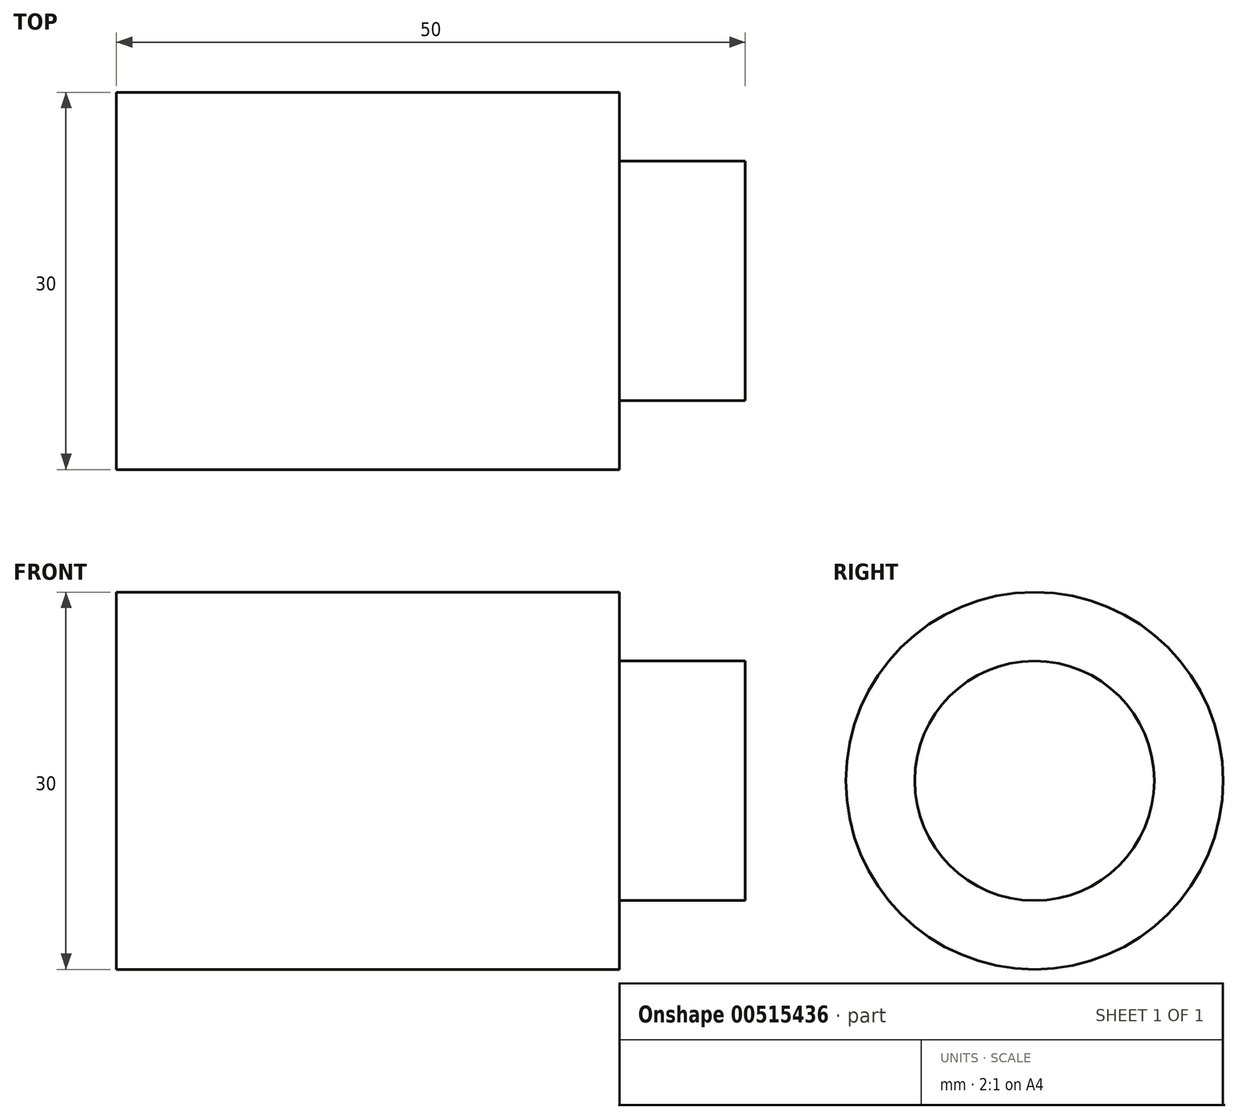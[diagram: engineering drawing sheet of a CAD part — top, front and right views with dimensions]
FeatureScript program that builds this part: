
annotation { "Feature Type Name" : "Feature", "Feature Type Description" : "" }
export const myFeature = defineFeature(function(context is Context, id is Id, definition is map)
    precondition{}
    {
        {
            var Q0;
            Q0=qCreatedBy(makeId("Front.planeOp"),FACE);
            var sketch = newSketch(context, id + "F0", { "sketchPlane" : qUnion([Q0])});
            skLineSegment(sketch, "E0", {"start": v(0, 0) * mm, "end": v(0, 15) * mm});
            skLineSegment(sketch, "E1", {"start": v(0, 15) * mm, "end": v(40, 15) * mm});
            skLineSegment(sketch, "E2", {"start": v(40, 15) * mm, "end": v(40, 9.53) * mm});
            skLineSegment(sketch, "E3", {"start": v(40, 9.53) * mm, "end": v(50, 9.53) * mm});
            skLineSegment(sketch, "E4", {"start": v(50, 9.53) * mm, "end": v(50, 0) * mm});
            skLineSegment(sketch, "E5", {"start": v(0, 0) * mm, "end": v(50, 0) * mm});
            skSolve(sketch);
        }
        {
            var Q0;
            Q0=makeQuery(id+"F0.imprint","IMPRINT",FACE,{"disambiguationData":[TD([[makeQuery(id+"F0.imprint","IMPRINT",EDGE,{"derivedFrom":sQuery(id+"F0.wireOp",EDGE,"E0")}),-1.0]])]});
            var Q1;
            Q1=sQuery(id+"F0.wireOp",EDGE,"E5");
            revolve(context, id + "F1", {"entities" : qUnion([Q0]), "axis" : qUnion([Q1]), "revolveType" : RevolveType.FULL});
        }
    });
